# Revit family: Furniture_Office-Chairs_Flokk_HAG_SoFi_7200
name_source: partatom
category: Furniture
units: mm (PartAtom-declared; Revit-internal decimal feet)

## family parameters
Always vertical = Yes
Cut with Voids When Loaded = No
OmniClass Number = 23.40.20.14.14.11
OmniClass Title = Chairs
Room Calculation Point = No
Shared = No
Work Plane-Based = No

## types (1)
- HAG SoFi 7200
    AssetType = Movable
    BIMObjectName = Furniture_Office-Chairs_Flokk_HAG_SoFi_7200
    Brand = HAG
    Category = Task chairs
    Collection = HAG SoFi
    Color = Various
    Cost = 0 $
    Default Elevation = 0 mm  [stored 0 ft]
    Description = The HÅG SoFi 7200 has a medium-height backrest. HÅG in Balance® technology ensures more subconscious movement. Adjustable seat height and depth, and lumbar support. Available with HÅG SlideBack™ armrests which allow you to move closer to your desk, invite you to sit sideways or use the armrests as elbow support. The height, width and forward position of the armrests can easily be adjusted. The optional headrest provides support and rest for your shoulders, neck and head.
    Designer = Powerdesign AS
    DurationUnit = Year
    Features = HÅG in Balance® (balanced, flowing tilt function backwards and forwards)

Seat depth adjustment

Seat height adjustment

Adjustable lumbar support

Adjustable tilting resistance forwards and backwards

Lockable tilt

Five star aluminum base (730mm) available in black, silver or white, optionally in polished aluminium. Mechanism cover is black when ordering black base. It's light grey when ordering silver or white base. Please specify when placing your order

Castors for hard or soft flooring. Must be specified at time of order

200 mm lift (Seat height: 450-640mm)
    HighestSeatingHeight = 640 mm  [stored 2.09974 ft]
    IfcExportAs = IfcFurnishingElementType
    IfcExportType = CHAIR
    LowestSeatingHeight = 450 mm  [stored 1.47638 ft]
    MainColor = Various
    Manufacturer = Flokk
    ManufacturerName = Flokk
    ManufacturerURL = https://www.flokk.com
    Material = Textile, metal, plastic
    Model = HAG SoFi 7200
    ModelNumber = 7200
    NBSDescription = Office chairs
    NBSReference = 45-35-20/330
    Name = HAG_SoFi_7200
    NominalDepth = 670 mm  [stored 2.19816 ft]
    NominalHeight = 936 mm
    NominalLength = 670 mm  [stored 2.19816 ft]
    OfficeChairSecondaryMaterial = Stainless Steel AISI 304
    OffieChairTertiaryMaterial = Plastic Black
    ProductInformation = The HÅG SoFi 7200 has a medium-height backrest. HÅG in Balance® technology ensures more subconscious movement. Adjustable seat height and depth, and lumbar support. Available with HÅG SlideBack™ armrests which allow you to move closer to your desk, invite you to sit sideways or use the armrests as elbow support. The height, width and forward position of the armrests can easily be adjusted. The optional headrest provides support and rest for your shoulders, neck and head.
    Revision = 4
    SeatingHeight = 497 mm
    Shape = Sculptured
    ShareRecyclableMaterials = 96%
    ShareRecycledMaterials = 45%
    Size = 670x670x1045/1235mm
    URL = https://store.flokk.com
    Uniclass2 = Pr_40_50_12_57
    Uniclass2015Description = Office chairs
    Uniclass2015Reference = Pr_40_50_12_57
    Version = 2
    VersionDate = 11/11/2022
    WarrantyDurationUnit = Year
    Weight = 22.5 kg

note: [stored X ft] marks values corroborated as IEEE doubles in the binary element streams (Revit-internal decimal feet)

## geometry (parser evidence)
native form markers: Sweep x11
no freeform markers — native parametric forms only
